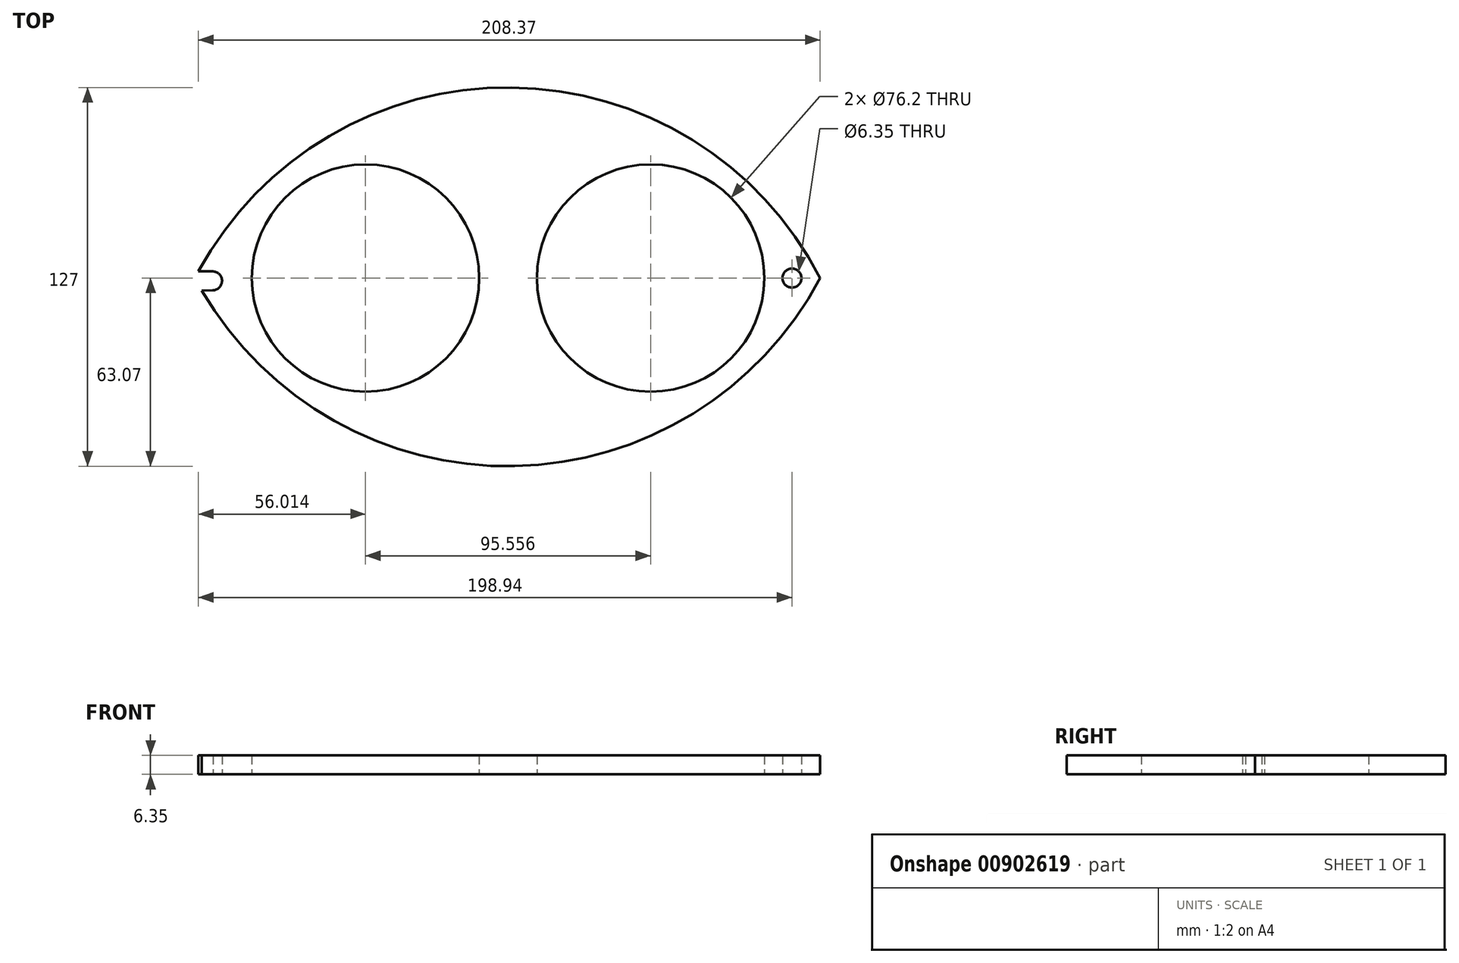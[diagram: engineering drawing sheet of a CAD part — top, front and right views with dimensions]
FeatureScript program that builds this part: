
annotation { "Feature Type Name" : "Feature", "Feature Type Description" : "" }
export const myFeature = defineFeature(function(context is Context, id is Id, definition is map)
    precondition{}
    {
        {
            var Q0;
            Q0=qCreatedBy(makeId("Top.planeOp"),FACE);
            var sketch = newSketch(context, id + "F0", { "sketchPlane" : qUnion([Q0])});
            skPoint(sketch, "E0.1.internal.snap0", {"position": v(131.27, 0) * mm});
            skArc(sketch, "E1", {"start": v(103.93, 0) * mm, "mid": v(-0.84, 63.93) * mm, "end": v(-105.62, 0) * mm});
            skArc(sketch, "E2", {"start": v(-105.62, 0) * mm, "mid": v(-0.84, -63.07) * mm, "end": v(103.93, 0) * mm});
            skCircle(sketch, "E3", {"center": v(94.5, 0) * mm, "radius": 3.18 * mm});
            skArc(sketch, "E4", {"start": v(-99.67, -4.11) * mm, "mid": v(-96.53, -1.02) * mm, "end": v(-99.5, 2.23) * mm});
            skLineSegment(sketch, "E5", {"start": v(-99.5, 2.23) * mm, "end": v(-104.44, 2.23) * mm});
            skLineSegment(sketch, "E6", {"start": v(-99.67, -4.11) * mm, "end": v(-103.3, -4.16) * mm});
            skArc(sketch, "E7", {"start": v(95.2, 0) * mm, "mid": v(-0.84, 58.15) * mm, "end": v(-96.89, 0) * mm});
            skArc(sketch, "E8", {"start": v(-96.89, 0) * mm, "mid": v(-0.84, -58.15) * mm, "end": v(95.2, 0) * mm});
            skLineSegment(sketch, "E9", {"start": v(0, 63.93) * mm, "end": v(0, -63.07) * mm, "construction": true});
            skCircle(sketch, "E10", {"center": v(-48.43, 0) * mm, "radius": 38.1 * mm});
            skCircle(sketch, "E11", {"center": v(47.13, 0) * mm, "radius": 38.1 * mm});
            skSolve(sketch);
        }
        {
            var Q0;
            {var subQ11=sQuery(id+"F0.wireOp",EDGE,"E5");Q0=makeQuery(id+"F0.imprint","IMPRINT",FACE,{"disambiguationData":[TD([[makeQuery(id+"F0.imprint","IMPRINT",EDGE,{"derivedFrom":subQ11}),-1.0]])]});}
            var Q1;
            Q1=makeQuery(id+"F0.imprint","IMPRINT",FACE,{"disambiguationData":[TD([[makeQuery(id+"F0.imprint","IMPRINT",EDGE,{"derivedFrom":sQuery(id+"F0.wireOp",EDGE,"E10")}),-1.0]])]});
            extrude(context, id + "F1", {"entities" : qUnion([Q0, Q1]), "depth" : 6.35 * mm, "offsetDistance" : 25.4 * mm});
        }
    });
